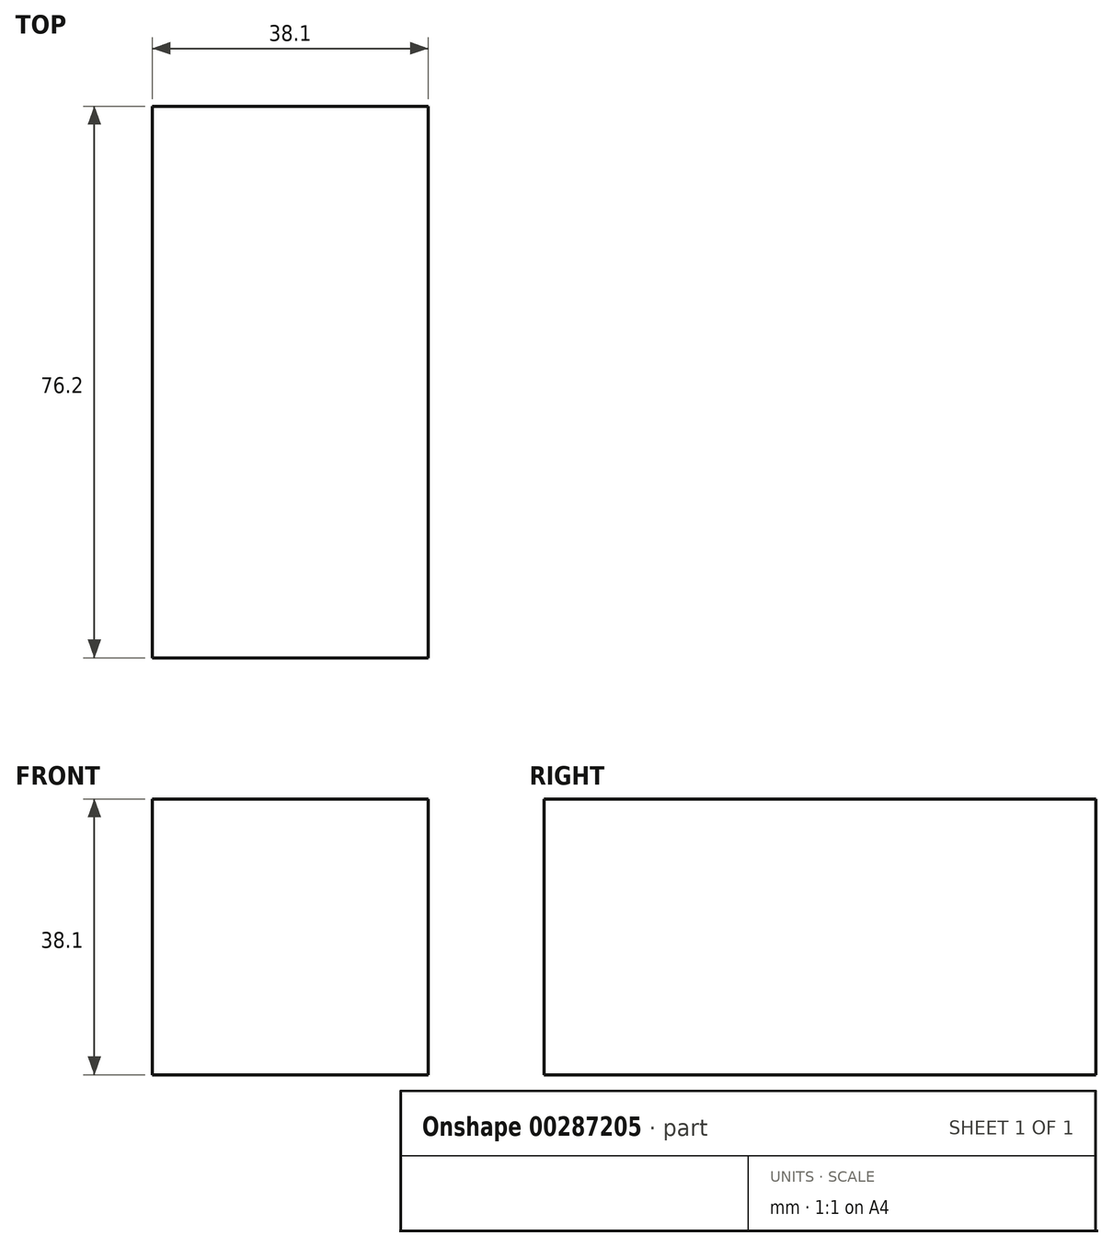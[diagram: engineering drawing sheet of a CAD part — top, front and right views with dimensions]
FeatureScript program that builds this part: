
annotation { "Feature Type Name" : "Feature", "Feature Type Description" : "" }
export const myFeature = defineFeature(function(context is Context, id is Id, definition is map)
    precondition{}
    {
        {
            var Q0;
            Q0=qCreatedBy(makeId("Front.planeOp"),FACE);
            var sketch = newSketch(context, id + "F0", { "sketchPlane" : qUnion([Q0])});
            skLineSegment(sketch, "E0.bottom", {"start": v(0, 0) * mm, "end": v(-38.1, 0) * mm});
            skLineSegment(sketch, "E0.top", {"start": v(0, 38.1) * mm, "end": v(-38.1, 38.1) * mm});
            skLineSegment(sketch, "E0.left", {"start": v(0, 0) * mm, "end": v(0, 38.1) * mm});
            skLineSegment(sketch, "E0.right", {"start": v(-38.1, 0) * mm, "end": v(-38.1, 38.1) * mm});
            skSolve(sketch);
        }
        {
            var Q0;
            Q0 = qSketchRegion(id + "F0", true);
            extrude(context, id + "F1", {"entities" : qUnion([Q0]), "depth" : 76.2 * mm});
        }
    });
